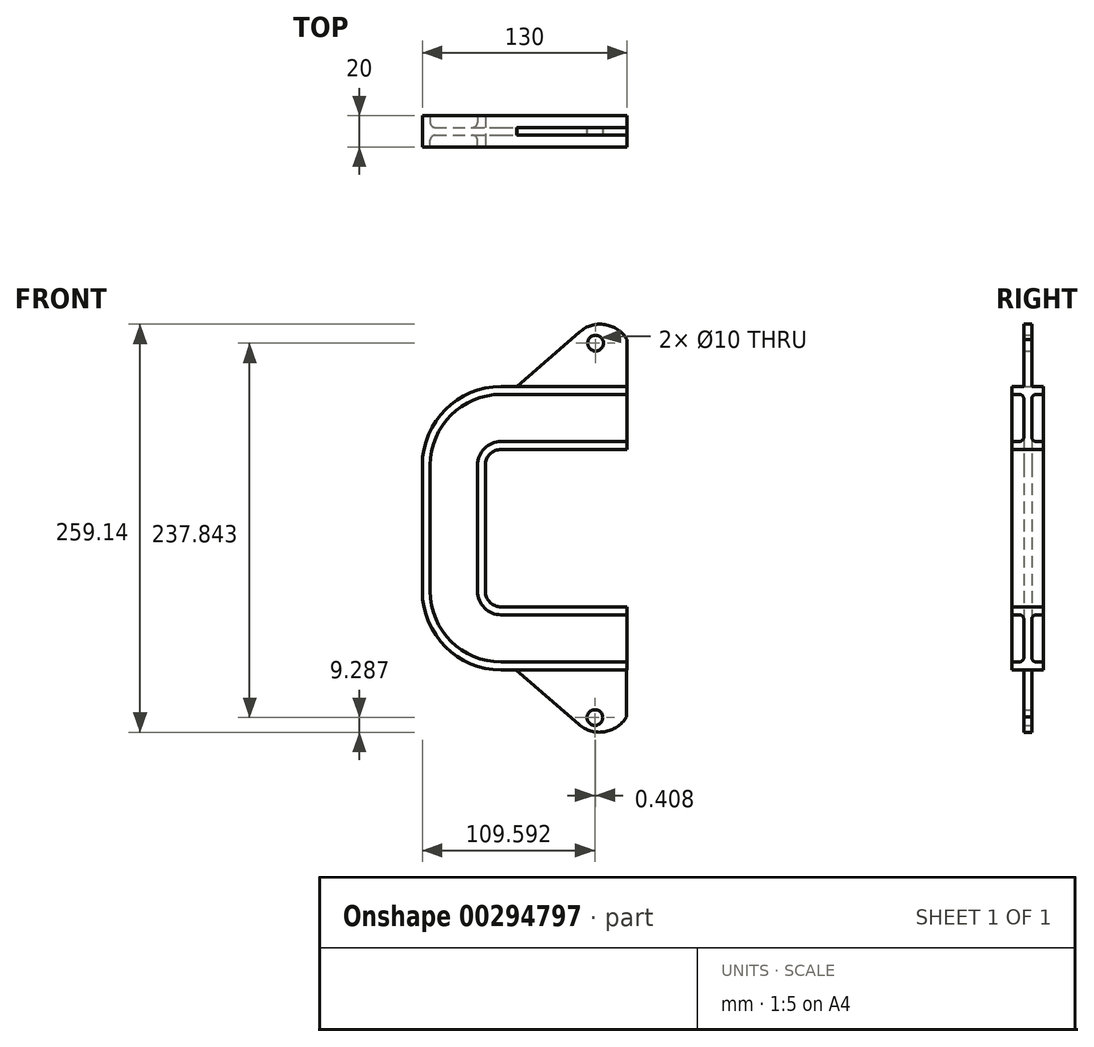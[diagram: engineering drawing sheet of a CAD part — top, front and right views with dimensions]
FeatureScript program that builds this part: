
annotation { "Feature Type Name" : "Feature", "Feature Type Description" : "" }
export const myFeature = defineFeature(function(context is Context, id is Id, definition is map)
    precondition{}
    {
        {
            var Q0;
            Q0=qCreatedBy(makeId("Right.planeOp"),FACE);
            var sketch = newSketch(context, id + "F0", { "sketchPlane" : qUnion([Q0])});
            skLineSegment(sketch, "E0", {"start": v(0, 20) * mm, "end": v(10, 20) * mm});
            skLineSegment(sketch, "E1", {"start": v(10, 20) * mm, "end": v(10, 15) * mm});
            skLineSegment(sketch, "E2", {"start": v(10, 15) * mm, "end": v(5.5, 15) * mm});
            skLineSegment(sketch, "E3", {"start": v(2.5, 12) * mm, "end": v(2.5, 0) * mm});
            skLineSegment(sketch, "E4.MirrorCS", {"start": v(10, -20) * mm, "end": v(10, -15) * mm});
            skLineSegment(sketch, "E5.MirrorCS", {"start": v(10, -15) * mm, "end": v(5.5, -15) * mm});
            skLineSegment(sketch, "E6.MirrorCS", {"start": v(0, -20) * mm, "end": v(10, -20) * mm});
            skLineSegment(sketch, "E7.MirrorCS", {"start": v(2.5, -12) * mm, "end": v(2.5, 0) * mm});
            skLineSegment(sketch, "E8.MirrorCS", {"start": v(-10, 20) * mm, "end": v(-10, 15) * mm});
            skLineSegment(sketch, "E9.MirrorCS", {"start": v(-10, -20) * mm, "end": v(-10, -15) * mm});
            skLineSegment(sketch, "E10.MirrorCS", {"start": v(-2.5, -12) * mm, "end": v(-2.5, 0) * mm});
            skLineSegment(sketch, "E11.MirrorCS", {"start": v(0, -20) * mm, "end": v(-10, -20) * mm});
            skLineSegment(sketch, "E12.MirrorCS", {"start": v(0, 20) * mm, "end": v(-10, 20) * mm});
            skLineSegment(sketch, "E13.MirrorCS", {"start": v(-10, -15) * mm, "end": v(-5.5, -15) * mm});
            skLineSegment(sketch, "E14.MirrorCS", {"start": v(-2.5, 12) * mm, "end": v(-2.5, 0) * mm});
            skLineSegment(sketch, "E15.MirrorCS", {"start": v(-10, 15) * mm, "end": v(-5.5, 15) * mm});
            skPoint(sketch, "E16.visualSharp", {"position": v(2.5, -15) * mm});
            skArc(sketch, "E16.filletArc", {"start": v(2.5, -12) * mm, "mid": v(3.38, -14.12) * mm, "end": v(5.5, -15) * mm});
            skPoint(sketch, "E17.visualSharp", {"position": v(-2.5, -15) * mm});
            skArc(sketch, "E17.filletArc", {"start": v(-5.5, -15) * mm, "mid": v(-3.38, -14.12) * mm, "end": v(-2.5, -12) * mm});
            skPoint(sketch, "E18.visualSharp", {"position": v(-2.5, 15) * mm});
            skArc(sketch, "E18.filletArc", {"start": v(-2.5, 12) * mm, "mid": v(-3.38, 14.12) * mm, "end": v(-5.5, 15) * mm});
            skPoint(sketch, "E19.visualSharp", {"position": v(2.5, 15) * mm});
            skArc(sketch, "E19.filletArc", {"start": v(5.5, 15) * mm, "mid": v(3.38, 14.12) * mm, "end": v(2.5, 12) * mm});
            skSolve(sketch);
        }
        {
            var Q0;
            Q0=qCreatedBy(makeId("Front.planeOp"),FACE);
            var sketch = newSketch(context, id + "F1", { "sketchPlane" : qUnion([Q0])});
            skLineSegment(sketch, "E20", {"start": v(0, 0) * mm, "end": v(-80, 0) * mm});
            skLineSegment(sketch, "E21", {"start": v(-110, -30) * mm, "end": v(-110, -110) * mm});
            skLineSegment(sketch, "E22", {"start": v(-80, -140) * mm, "end": v(0, -140) * mm});
            skPoint(sketch, "E23.visualSharp", {"position": v(-110, 0) * mm});
            skArc(sketch, "E23.filletArc", {"start": v(-80, 0) * mm, "mid": v(-101.21, -8.79) * mm, "end": v(-110, -30) * mm});
            skPoint(sketch, "E24.visualSharp", {"position": v(-110, -140) * mm});
            skArc(sketch, "E24.filletArc", {"start": v(-110, -110) * mm, "mid": v(-101.21, -131.21) * mm, "end": v(-80, -140) * mm});
            skSolve(sketch);
        }
        {
            var Q0;
            Q0=makeQuery(id+"F0.imprint","IMPRINT",FACE,{"disambiguationData":[TD([[makeQuery(id+"F0.imprint","IMPRINT",EDGE,{"derivedFrom":sQuery(id+"F0.wireOp",EDGE,"E0")}),-1.0]])]});
            var Q1;
            Q1 = qConstructionFilter(qBodyType(qCreatedBy(id + "F1" ,EDGE), BodyType.WIRE), ConstructionObject.NO);
            sweep(context, id + "F2", {"profiles" : qUnion([Q0]), "path" : qUnion([Q1])});
        }
        {
            var Q0;
            Q0=qCreatedBy(makeId("Front.planeOp"),FACE);
            var sketch = newSketch(context, id + "F3", { "sketchPlane" : qUnion([Q0])});
            skLineSegment(sketch, "E25", {"start": v(0, 20) * mm, "end": v(0, 50) * mm});
            skLineSegment(sketch, "E26", {"start": v(-30.16, 54.68) * mm, "end": v(-70, 20) * mm});
            skLineSegment(sketch, "E27", {"start": v(-70, 20) * mm, "end": v(0, 20) * mm});
            skCircle(sketch, "E28", {"center": v(-20, 47.56) * mm, "radius": 5 * mm});
            skArc(sketch, "E29", {"start": v(0, 50) * mm, "mid": v(-14, 59.33) * mm, "end": v(-30.16, 54.68) * mm});
            skLineSegment(sketch, "E30", {"start": v(-70.4, -160) * mm, "end": v(-0.4, -160) * mm});
            skArc(sketch, "E31.MirrorCS", {"start": v(-0.4, -190) * mm, "mid": v(-14.45, -199.34) * mm, "end": v(-30.64, -194.62) * mm});
            skCircle(sketch, "E32.MirrorC", {"center": v(-20.4, -190.28) * mm, "radius": 5 * mm});
            skLineSegment(sketch, "E33.MirrorCS", {"start": v(-0.4, -160) * mm, "end": v(-0.4, -190) * mm});
            skLineSegment(sketch, "E34.MirrorCS", {"start": v(-30.64, -194.62) * mm, "end": v(-70.4, -160) * mm});
            skSolve(sketch);
        }
        {
            var Q0;
            Q0=makeQuery(id+"F3.imprint","IMPRINT",FACE,{"disambiguationData":[TD([[makeQuery(id+"F3.imprint","IMPRINT",EDGE,{"derivedFrom":sQuery(id+"F3.wireOp",EDGE,"E25")}),1.0]])]});
            extrude(context, id + "F4", {"entities" : qUnion([Q0]), "operationType" : NewBodyOperationType.ADD, "endBound" : BoundingType.SYMMETRIC, "depth" : 5 * mm});
        }
        {
            var Q0;
            Q0 = qSketchRegion(id + "F3", true);
            extrude(context, id + "F5", {"entities" : qUnion([Q0]), "operationType" : NewBodyOperationType.ADD, "endBound" : BoundingType.SYMMETRIC, "depth" : 5 * mm});
        }
    });
